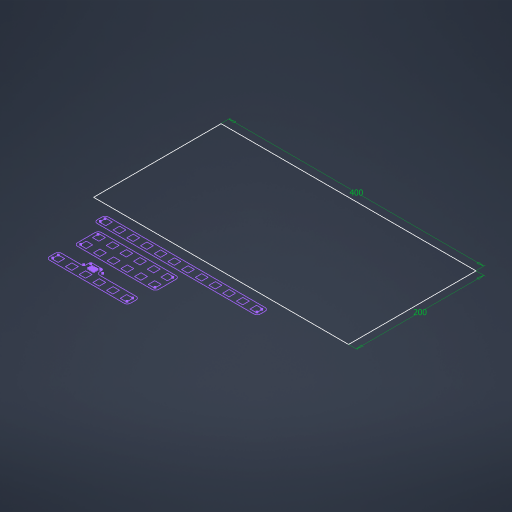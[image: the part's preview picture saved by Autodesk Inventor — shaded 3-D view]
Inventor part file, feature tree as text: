
AUTODESK INVENTOR PART (.ipt)
format: ipt  version: 2024.3 (Build 283343010, 343A)  size: 279,552 bytes
history: native  units: mm
features: sketch x1
ambient origin geometry x8: Origin, YZ Plane, XZ Plane, XY Plane, X Axis, Y Axis, Z Axis, Center Point
feature tree (1):
  sketch  "Skizze1"  dims[d2=400.0mm d3=200.0mm]
